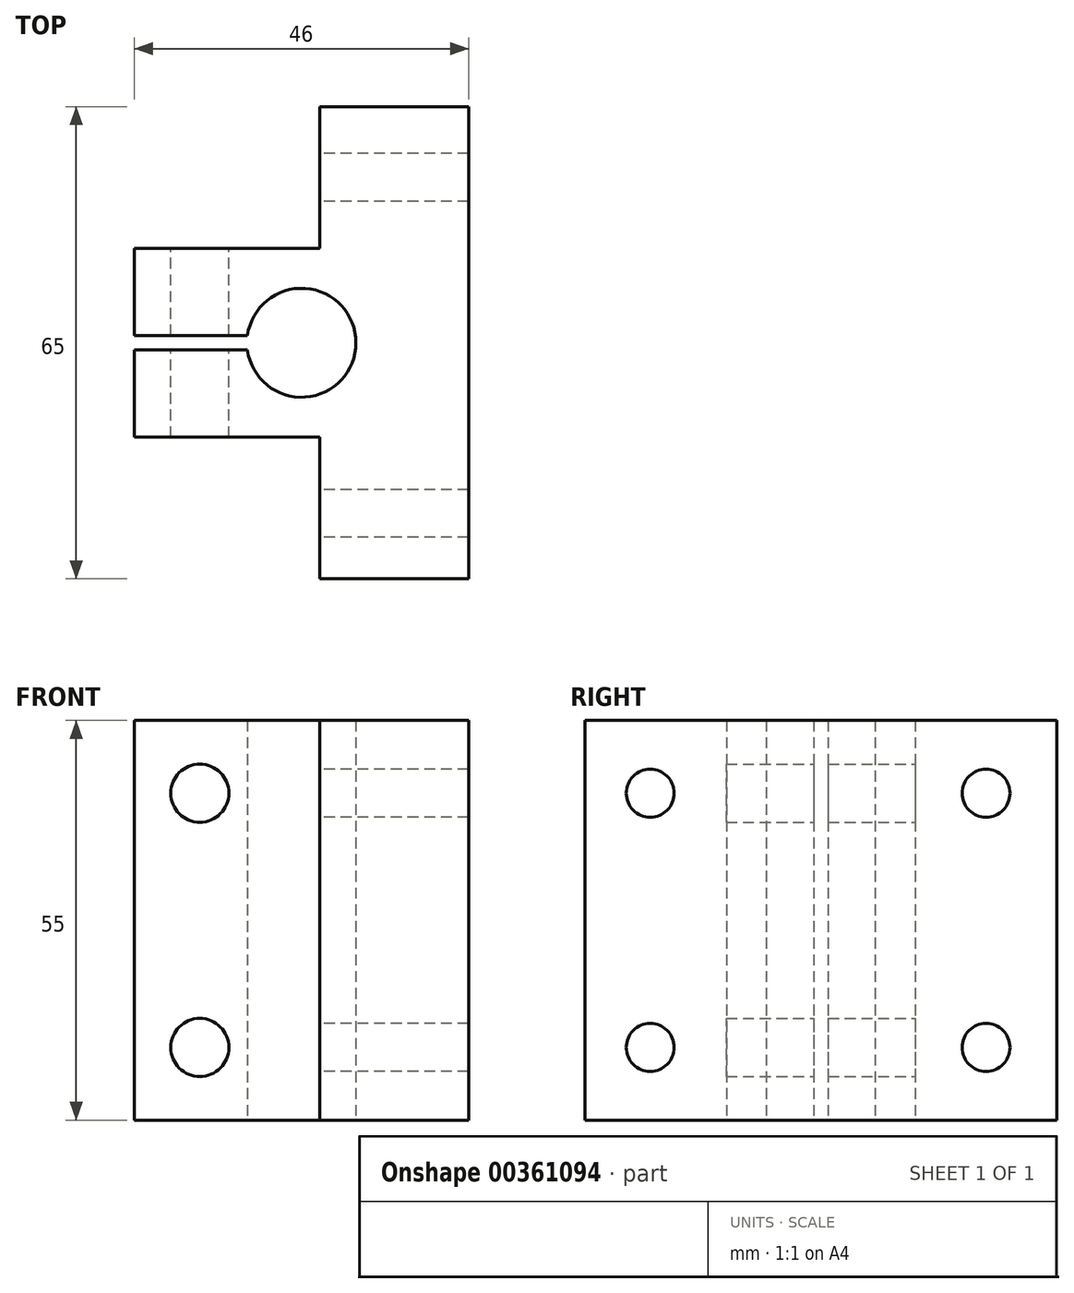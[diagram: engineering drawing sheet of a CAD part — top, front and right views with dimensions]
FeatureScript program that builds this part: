
annotation { "Feature Type Name" : "Feature", "Feature Type Description" : "" }
export const myFeature = defineFeature(function(context is Context, id is Id, definition is map)
    precondition{}
    {
        {
            var Q0;
            Q0=qCreatedBy(makeId("Top.planeOp"),FACE);
            var sketch = newSketch(context, id + "F0", { "sketchPlane" : qUnion([Q0])});
            skLineSegment(sketch, "E0", {"start": v(58.6, 55.99) * mm, "end": v(58.6, -9.01) * mm});
            skLineSegment(sketch, "E1", {"start": v(58.6, 55.99) * mm, "end": v(38.1, 55.99) * mm});
            skLineSegment(sketch, "E2", {"start": v(38.1, 55.99) * mm, "end": v(38.1, 36.49) * mm});
            skLineSegment(sketch, "E3", {"start": v(38.1, 36.49) * mm, "end": v(12.6, 36.49) * mm});
            skLineSegment(sketch, "E4", {"start": v(58.6, -9.01) * mm, "end": v(38.1, -9.01) * mm});
            skLineSegment(sketch, "E5", {"start": v(38.1, -9.01) * mm, "end": v(38.1, 10.49) * mm});
            skLineSegment(sketch, "E6", {"start": v(38.1, 10.49) * mm, "end": v(12.6, 10.49) * mm});
            skLineSegment(sketch, "E7", {"start": v(12.6, 10.49) * mm, "end": v(12.6, 22.49) * mm});
            skLineSegment(sketch, "E8", {"start": v(12.6, 36.49) * mm, "end": v(12.6, 24.49) * mm});
            skLineSegment(sketch, "E9", {"start": v(12.6, 24.49) * mm, "end": v(28.16, 24.49) * mm});
            skLineSegment(sketch, "E10", {"start": v(12.6, 22.49) * mm, "end": v(28.16, 22.49) * mm});
            skArc(sketch, "E11", {"start": v(28.16, 22.49) * mm, "mid": v(43.1, 23.49) * mm, "end": v(28.16, 24.49) * mm});
            skPoint(sketch, "E12.orphan", {"position": v(35.6, 22.49) * mm});
            skPoint(sketch, "E13.end.orphan", {"position": v(35.6, 24.49) * mm});
            skSolve(sketch);
        }
        {
            var Q0;
            Q0=qSketchRegion(id+"F0",true);
            extrude(context, id + "F1", {"entities" : qUnion([Q0]), "depth" : 55 * mm});
        }
        {
            var Q0;
            Q0=makeQuery(id+"F1.opExtrude","SWEPT_FACE",FACE,{"disambiguationData":[OSD([sQuery(id+"F0.wireOp",EDGE,"E3")])]});
            var sketch = newSketch(context, id + "F2", { "sketchPlane" : qUnion([Q0])});
            skLineSegment(sketch, "E14", {"start": v(-12.6, 0) * mm, "end": v(-12.6, 10) * mm});
            skLineSegment(sketch, "E15", {"start": v(-12.6, 10) * mm, "end": v(-21.6, 10) * mm});
            skLineSegment(sketch, "E16", {"start": v(-21.6, 55) * mm, "end": v(-21.6, 45) * mm});
            skCircle(sketch, "E17", {"center": v(-21.6, 10) * mm, "radius": 4 * mm});
            skCircle(sketch, "E18", {"center": v(-21.6, 45) * mm, "radius": 4 * mm});
            skSolve(sketch);
        }
        {
            var Q0;
            Q0=makeQuery(id+"F2.imprint","IMPRINT",FACE,{"disambiguationData":[TD([[makeQuery(id+"F2.imprint","IMPRINT",EDGE,{"derivedFrom":sQuery(id+"F2.wireOp",EDGE,"E17")}),1.0]])]});
            var Q1;
            Q1=makeQuery(id+"F2.imprint","IMPRINT",FACE,{"disambiguationData":[TD([[makeQuery(id+"F2.imprint","IMPRINT",EDGE,{"derivedFrom":sQuery(id+"F2.wireOp",EDGE,"E18")}),1.0]])]});
            extrude(context, id + "F3", {"entities" : qUnion([Q0, Q1]), "operationType" : NewBodyOperationType.REMOVE, "oppositeDirection" : true, "depth" : 29.3 * mm});
        }
        {
            var Q0;
            Q0=makeQuery(id+"F1.opExtrude","SWEPT_FACE",FACE,{"disambiguationData":[OSD([sQuery(id+"F0.wireOp",EDGE,"E5")])]});
            var sketch = newSketch(context, id + "F4", { "sketchPlane" : qUnion([Q0])});
            skLineSegment(sketch, "E19", {"start": v(0, 55) * mm, "end": v(0, 45) * mm});
            skCircle(sketch, "E20", {"center": v(0, 45) * mm, "radius": 3.3 * mm});
            skLineSegment(sketch, "E21", {"start": v(0, 0) * mm, "end": v(0, 10) * mm});
            skCircle(sketch, "E22", {"center": v(0, 10) * mm, "radius": 3.3 * mm});
            skSolve(sketch);
        }
        {
            var Q0;
            Q0=makeQuery(id+"F4.imprint","IMPRINT",FACE,{"disambiguationData":[TD([[makeQuery(id+"F4.imprint","IMPRINT",EDGE,{"derivedFrom":sQuery(id+"F4.wireOp",EDGE,"E20")}),1.0]])]});
            var Q1;
            Q1=makeQuery(id+"F4.imprint","IMPRINT",FACE,{"disambiguationData":[TD([[makeQuery(id+"F4.imprint","IMPRINT",EDGE,{"derivedFrom":sQuery(id+"F4.wireOp",EDGE,"E22")}),1.0]])]});
            extrude(context, id + "F5", {"entities" : qUnion([Q0, Q1]), "operationType" : NewBodyOperationType.REMOVE, "oppositeDirection" : true, "depth" : 33.2 * mm});
        }
        {
            var Q0;
            Q0=makeQuery(id+"F1.opExtrude","SWEPT_FACE",FACE,{"disambiguationData":[OSD([sQuery(id+"F0.wireOp",EDGE,"E2")])]});
            var sketch = newSketch(context, id + "F6", { "sketchPlane" : qUnion([Q0])});
            skLineSegment(sketch, "E23", {"start": v(-46.24, 0) * mm, "end": v(-46.24, 10) * mm});
            skLineSegment(sketch, "E24", {"start": v(-46.24, 55) * mm, "end": v(-46.24, 45) * mm});
            skPoint(sketch, "E24.endSnap0", {"position": v(-46.24, 55) * mm});
            skCircle(sketch, "E25", {"center": v(-46.24, 45) * mm, "radius": 3.3 * mm});
            skCircle(sketch, "E26", {"center": v(-46.24, 10) * mm, "radius": 3.3 * mm});
            skLineSegment(sketch, "E27", {"start": v(-55.99, 55) * mm, "end": v(-46.24, 55) * mm});
            skLineSegment(sketch, "E28", {"start": v(-55.99, 0) * mm, "end": v(-46.24, 0) * mm});
            skSolve(sketch);
        }
        {
            var Q0;
            Q0=makeQuery(id+"F6.imprint","IMPRINT",FACE,{"disambiguationData":[TD([[makeQuery(id+"F6.imprint","IMPRINT",EDGE,{"derivedFrom":sQuery(id+"F6.wireOp",EDGE,"E25")}),1.0]])]});
            extrude(context, id + "F7", {"entities" : qUnion([Q0]), "operationType" : NewBodyOperationType.REMOVE, "oppositeDirection" : true, "depth" : 34.5 * mm});
        }
        {
            var Q0;
            Q0=makeQuery(id+"F1.opExtrude","SWEPT_FACE",FACE,{"disambiguationData":[OSD([sQuery(id+"F0.wireOp",EDGE,"E2")])]});
            var sketch = newSketch(context, id + "F8", { "sketchPlane" : qUnion([Q0])});
            skLineSegment(sketch, "E29", {"start": v(-46.24, 0) * mm, "end": v(-46.24, 10) * mm});
            skCircle(sketch, "E30", {"center": v(-46.24, 10) * mm, "radius": 3.3 * mm});
            skSolve(sketch);
        }
        {
            var Q0;
            Q0=makeQuery(id+"F8.imprint","IMPRINT",FACE,{"disambiguationData":[TD([[makeQuery(id+"F8.imprint","IMPRINT",EDGE,{"derivedFrom":sQuery(id+"F8.wireOp",EDGE,"E30")}),1.0]])]});
            var Q1;
            Q1=makeQuery(id+"F1.opExtrude","SWEPT_FACE",FACE,{"disambiguationData":[OSD([sQuery(id+"F0.wireOp",EDGE,"E0")])]});
            extrude(context, id + "F9", {"entities" : qUnion([Q0, Q1]), "operationType" : NewBodyOperationType.REMOVE, "oppositeDirection" : true, "depth" : 37.2 * mm});
        }
    });
